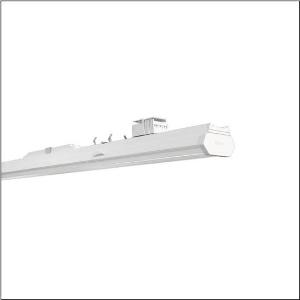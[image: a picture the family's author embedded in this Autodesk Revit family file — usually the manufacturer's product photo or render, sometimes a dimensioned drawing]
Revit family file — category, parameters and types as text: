
# Revit family: licross_21_protected_mo_52td12dn4a5g3c
name_source: partatom
category: Lighting Fixtures
units: mm (PartAtom-declared; Revit-internal decimal feet)

## family parameters
Cut with Voids When Loaded = No
Host = Face
Light Source = No
Part Type = Normal
Room Calculation Point = No
Round Connector Dimension = Use Diameter
Shared = No

## types (1)
- --- (1 x LED, 940 lm, 6.8 W, 4000K)
    Apparent Load = 7 VA
    CIE Flux Codes = 73 92 98 99 100
    Color Rendering = 80
    Color Temperature = 4000K
    Default Elevation = 1800 mm
    Description = Licross 21 Protected MO, luminaire insert, of sheet steel, galvanised, coil coated, white, length: 1.500mm, width: 90mm, height: 103mm, LED rated luminous flux: 10.700lm, light colour: 840, SDCM (Standard Deviation of Colour Matching)MacAdam ≤ 3 SDCM (initial), control gear: DALI 2 (for two DALI lines), with plug, 6-pole, with phase selection, for trunking rail, 14-core, mains connection: 220..240V, AC, 50/60Hz, rated input power: 66W, for trunking rail, 14-core, internal wiring halogen-free, for emergency light function, converter,control gear: single battery element, battery: LiFePO4, 9Ah, primary light control with lens, of plastic, primary optical cover: cover, of PMMA, light emission: direct distribution, primary light characteristic: symmetric, protection rating (complete): IP54, insulation class (complete): insulation class I (protective earthing), certification: CE, UKCA, protection symbol: D if used in an environment with non-conductive dust loads with corresponding accessories, impact resistance: IK06, permissible ambient temperature for indoor applications: +5..+35°C, standard: EN 60598-2-22, LABS conformity tested according to VDMA 24364:2018-05, reducing of maximum allowable ambient temperature of 5°C with ceiling mounting, corresponds to IFS (International Featured Standards) requirements for safety and quality in the food industry, The light source and the operating device comply with the requirements of the Ecodesign Regulation (EU) 2019/2020 and are replaceable in accordance with this regulation, packaging unit: 1 piece
    Height = 92 mm
    Lamp = 1 x LED
    Lamp Light Flux = 940 lm
    Lamp Power = 6.8 W
    Lamp count = 1
    Length = 1500 mm
    Luminous efficacy = 138 lm/W
    Manufacturer = Siteco
    ModVariant = No
    Model = 52TD12DN4A5G3C
    Mounting Place = Ceiling
    Mounting Type = Pendant
    Number of Poles = 1
    OnlyDefault = Yes
    Power Factor = 1
    Product Name = Licross 21 Protected MO
    Product group = luminaire insert | ceiling pendant
    ProductGroupID = 901
    Protection Class = Protection class I
    Protection Degree = IP 54
    RLX_Detail_Level = 1
    RLX_Emergency_Light_Flux = 0 lm
    RLX_Emergency_Type = 0
    RLX_Emergency_Type_DB = No
    RlxData = <blob elided: 25077 chars, md5=a599ff52>
    Socket = socket
    Standby Power = 0 W
    System Light Flux = 940 lm
    System Power = 7 W
    Type Comments = : emergency light operation: 3 h
    Type Image = l_1256148.jpg
    URL = http://relux.com
    VarID = @adj_112435
    Voltage = 0 V
    Weight = 0.00 kg
    Width = 88 mm

## geometry (parser evidence)
native form markers: Blend x4, Sweep x11
no freeform markers — native parametric forms only
